# Revit family: 1STERN_FAUCET_TOUCHLESS_CLASSIC_CS
name_source: partatom
category: Generic Models
revit_build: Autodesk Revit 2017 (Build: 20160225_1515(x64)
units: mm (PartAtom-declared; Revit-internal decimal feet)

## family parameters
Can host rebar = No
Cut with Voids When Loaded = No
Host = Face
Part Type = Normal
Room Calculation Point = Yes
Round Connector Dimension = Use Diameter
Shared = No

## types (2) — shared parameters
AVAILABLE FINISHES = Brushed Nickel - Matt Black - Satin Gold - PVD Antique Bronze - PVD rose Gold - PVD Copper - AISI316 Material
BADGE = https://bim.archiproducts.com
DEPTH = 190 mm
Default Elevation = 1219 mm
Description = CLASSIC CS - Touch-free electronic faucet for deck-mounted installations.‎ Activated by concealed sensor built into the spout.‎ Solid brass one-piece construction.‎ For cold or premixed water.‎ Filter included.‎ Latching solenoid valve is located externally below the deck.‎ Sensor includes a low battery indicator.‎ Adjustable settings by remote control: sensor range, security time, delay in, delay out, on-off and reset to factory settings.‎
FINISHING MATERIAL = Chrome - Stern
HEIGHT = 160 mm
INSTALLATION = Lavatory mounted
MATERIAL DESCRIPTION = Finish: Chrome
Manufacturer = Stern Engineering
OPERATING PRESSURE = 0.5 - 8.0 BAR (7- 116  PSI)
OPTIONS = Remote control (code 07100005), Matching battery-powered soap dispenser (code 292400), Matching transformer-powered soap dispenser combination (code 292410)
PRODUCT SHEET = https://www.archiproducts.com
SECURITY TIME = Auto shutoff after 90 seconds. Adjustableby remote control.
TECHNICAL SHEET = http://www.sternfaucets.com
URL = http://www.sternfaucets.com
VOLTAGE = 9 V
WATER FLOW = 5.7 LPM
WATER SAVING OPTIONS = 1.89 LPM/0.5 GPM - PCA spray
WATER SUPPLY = Cold or premixed water
WATER TEMPERATURE = 70°C Maximum
WIDTH = 60 mm

## per-type parameters (varying)
| type | Model | POWER SUPPLY | PRODUCT CODE |
| CLASSIC_CS - 9V BATTERY | Classic CS B | 9V Battery | 293100 |
| CLASSIC_CS - 9V TRANSFORMER | Classic CS E | 9V Transformer | 293200 |

## geometry (parser evidence)
native form markers: Blend x4, Sweep x2
no freeform markers — native parametric forms only
